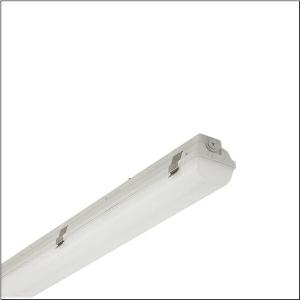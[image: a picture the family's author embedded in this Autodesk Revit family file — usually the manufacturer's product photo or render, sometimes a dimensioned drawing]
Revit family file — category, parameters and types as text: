
# Revit family: monsun_r__21_eco_51fj10ml45a_013e
name_source: partatom
category: Lighting Fixtures
units: mm (PartAtom-declared; Revit-internal decimal feet)

## family parameters
Cut with Voids When Loaded = No
Host = Face
Light Source = No
Part Type = Normal
Room Calculation Point = No
Round Connector Dimension = Use Diameter
Shared = No

## types (1)
- --- (1 x LED, 5000 lm, 36 W, 4000K)
    Apparent Load = 36 VA
    CIE Flux Codes = 41 70 89 90 100
    Color Rendering = 80
    Color Temperature = 4000K
    Default Elevation = 1800 mm
    Description = Monsun® 21 Eco, damp-proof luminaire, primary optical cover: diffuser, of PMMA, frosted, light emission: direct distribution, primary light characteristic: symmetric, installation type: suspended mounting, surface-mounted, LED, rated luminous flux: 5.000lm, luminous efficacy: 139lm/W, light colour: 840, colour temperature: 4000K, control gear: ECG Multilumen, with terminal, 3-pole, max. 2.5mm², mains connection: 220..240V, AC, 50/60Hz, rated input power: 36W, housing, of glass-fibre reinforced polyester, light grey (RAL 7035), length: 1.277mm, width: 90mm, height: 95mm, clip for enclosure, of spring steel V2A, protection rating (complete): IP66, insulation class (complete): insulation class I (protective earthing), certification: CE, UKCA, protection symbol: D, impact resistance: IK02, permissible operating ambient temperature: -20..+35°C, corresponds to IFS (International Featured Standards) requirements for safety and quality in the food industry, contact your sales advisor before using the luminaires in applications with unclear chemical exposure, large temperature fluctuations or condensation-forming humidity, packaging unit: 1 piece
    Height = 103 mm
    Lamp = 1 x LED
    Lamp Light Flux = 5000 lm
    Lamp Power = 36 W
    Lamp count = 1
    Length = 1277 mm
    Luminous efficacy = 139 lm/W
    Manufacturer = Siteco
    ModVariant = No
    Model = 51FJ10ML45A
    Mounting Place = Ceiling
    Mounting Type = Surface mounted
    Number of Poles = 1
    OnlyDefault = Yes
    Power Factor = 1
    Product Name = Monsun® 21 Eco
    Product group = damp-proof luminaire
    ProductGroupID = 300
    Protection Class = Protection class I
    Protection Degree = IP 66
    RLX_Detail_Level = 1
    RLX_Emergency_Light_Flux = 0 lm
    RLX_Emergency_Type = 0
    RLX_Emergency_Type_DB = No
    RlxData = <blob elided: 34049 chars, md5=bddb2bd6>
    Socket = socket
    Standby Power = 0 W
    System Light Flux = 5000 lm
    System Power = 36 W
    Type Comments = factory setting: luminous flux: 100 % | (ON | ON | ON | ON) | 350 mA
    Type Image = l_1007218.jpg
    URL = http://relux.com
    VarID = @adj_077829
    Voltage = 0 V
    Weight = 0.00 kg
    Width = 90 mm

## geometry (parser evidence)
native form markers: Blend x4, Sweep x12
no freeform markers — native parametric forms only
